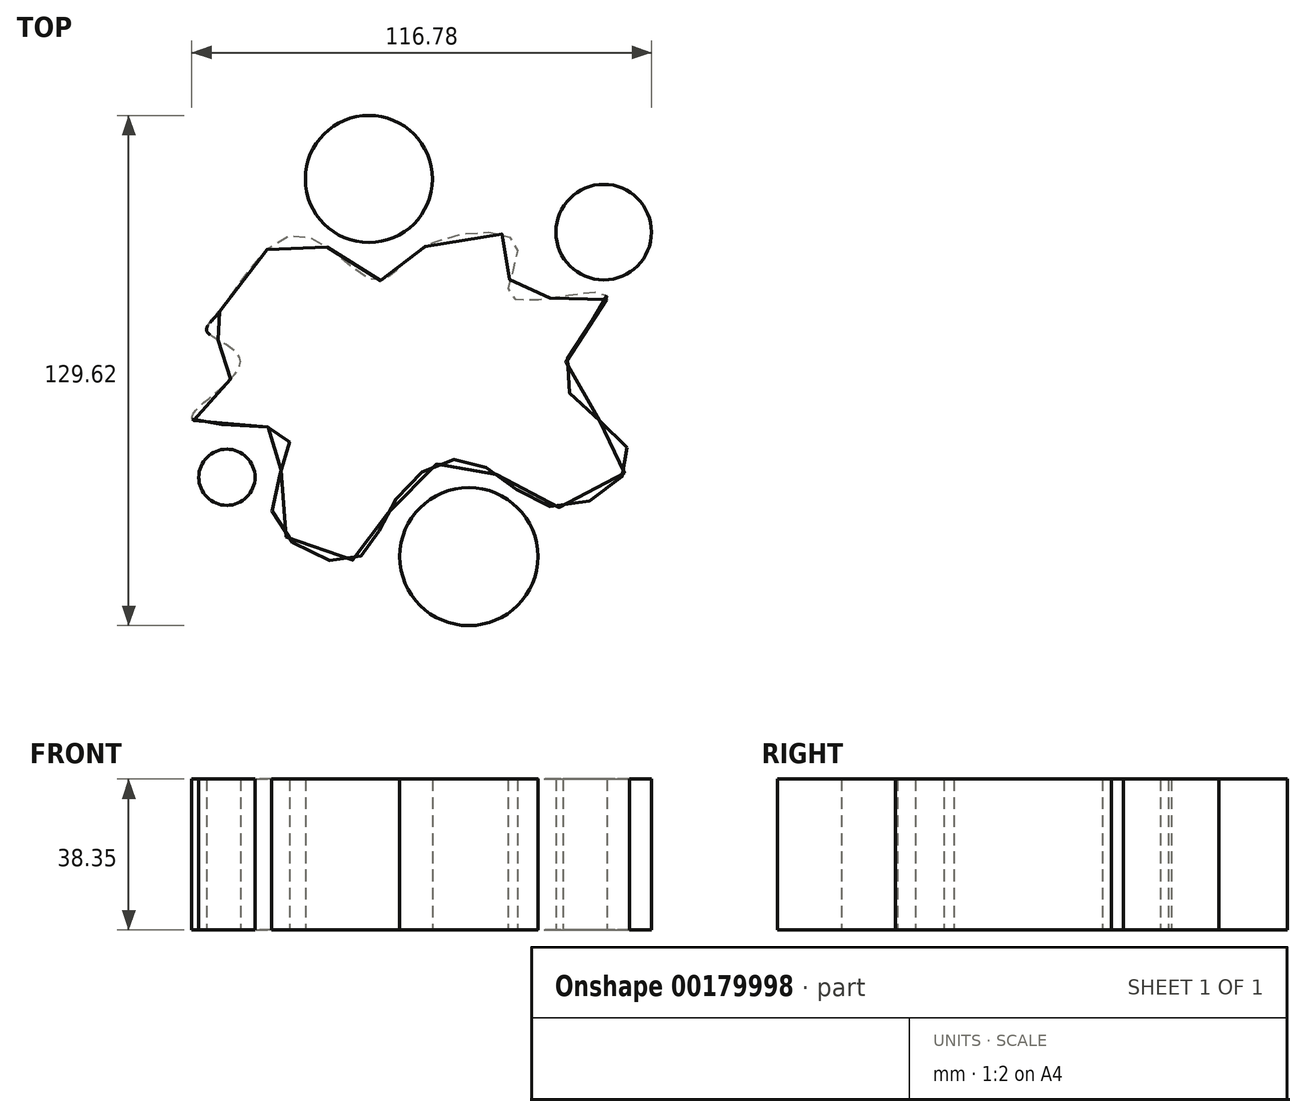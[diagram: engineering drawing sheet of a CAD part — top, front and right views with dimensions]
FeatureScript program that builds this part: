
annotation { "Feature Type Name" : "Feature", "Feature Type Description" : "" }
export const myFeature = defineFeature(function(context is Context, id is Id, definition is map)
    precondition{}
    {
        {
            var Q0;
            Q0=qCreatedBy(makeId("Top.planeOp"),FACE);
            var sketch = newSketch(context, id + "F0", { "sketchPlane" : qUnion([Q0])});
            skFitSpline(sketch, "E0", {"points": [v(-53.6, 21.77) * mm, v(-34.26, 41.31) * mm, v(-14.1, 29.63) * mm, v(-1.81, 38.1) * mm, v(21.77, 38.7) * mm, v(20.36, 25.4) * mm, v(44.54, 26.2) * mm, v(33.66, 5.44) * mm, v(50.38, -14.3) * mm, v(32.45, -28.01) * mm, v(10.08, -16.12) * mm, v(-8.67, -25.6) * mm, v(-20.15, -41.52) * mm, v(-40.3, -29.02) * mm, v(-36.88, -9.27) * mm, v(-60.66, -5.44) * mm, v(-48.37, 8.67) * mm, v(-56.63, 16.32) * mm, v(-53.6, 21.77) * mm]});
            skCircle(sketch, "E1", {"center": v(-15.72, 55.42) * mm, "radius": 16.15 * mm});
            skCircle(sketch, "E2", {"center": v(43.93, 41.92) * mm, "radius": 12.13 * mm});
            skCircle(sketch, "E3", {"center": v(9.67, -40.5) * mm, "radius": 17.54 * mm});
            skCircle(sketch, "E4", {"center": v(-51.8, -20.36) * mm, "radius": 7.14 * mm});
            skSolve(sketch);
        }
        {
            var Q0;
            Q0 = qSketchRegion(id + "F0", true);
            extrude(context, id + "F1", {"entities" : qUnion([Q0]), "depth" : 38.35 * mm});
        }
    });
